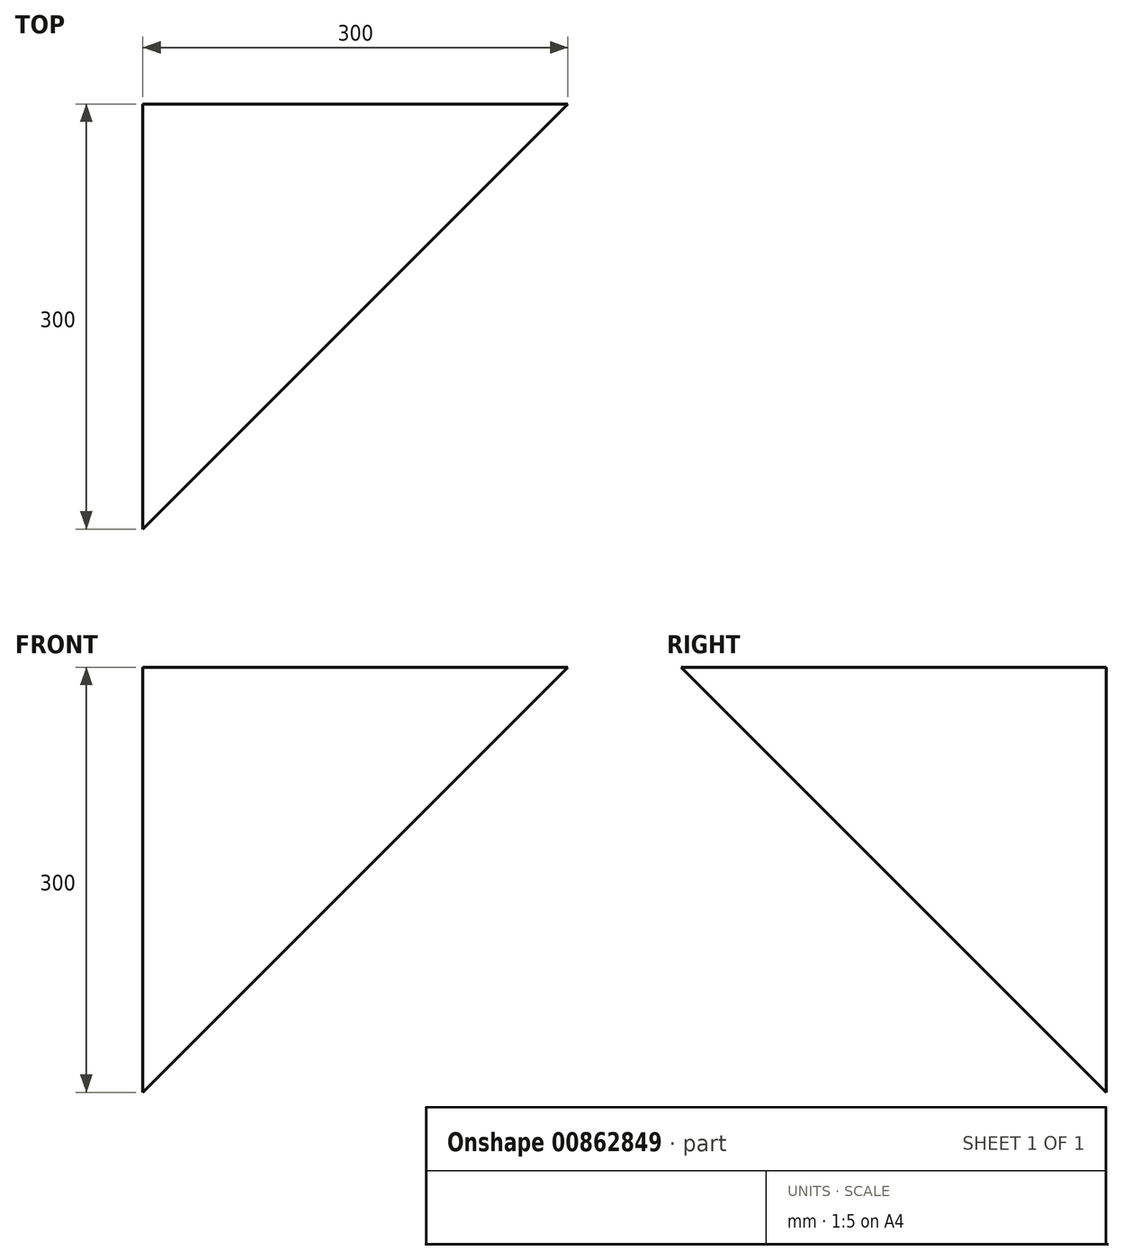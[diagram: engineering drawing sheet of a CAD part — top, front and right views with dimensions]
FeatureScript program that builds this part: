
annotation { "Feature Type Name" : "Feature", "Feature Type Description" : "" }
export const myFeature = defineFeature(function(context is Context, id is Id, definition is map)
    precondition{}
    {
        {
            var Q0;
            Q0=qCreatedBy(makeId("Top.planeOp"),FACE);
            var sketch = newSketch(context, id + "F0", { "sketchPlane" : qUnion([Q0])});
            skLineSegment(sketch, "E0.bottom", {"start": v(0, 0) * mm, "end": v(300, 0) * mm});
            skLineSegment(sketch, "E0.left", {"start": v(0, 0) * mm, "end": v(0, -300) * mm});
            skLineSegment(sketch, "E1", {"start": v(300, 0) * mm, "end": v(2300, 0) * mm});
            skLineSegment(sketch, "E2", {"start": v(0, -300) * mm, "end": v(0, -2300) * mm});
            skSolve(sketch);
        }
        {
            var Q0;
            Q0=qCreatedBy(makeId("Front.planeOp"),FACE);
            var sketch = newSketch(context, id + "F1", { "sketchPlane" : qUnion([Q0])});
            skLineSegment(sketch, "E3.0", {"start": v(0, 0) * mm, "end": v(300, 0) * mm});
            skLineSegment(sketch, "E4", {"start": v(0, 0) * mm, "end": v(0, -300) * mm});
            skLineSegment(sketch, "E5", {"start": v(0, -300) * mm, "end": v(0, -2300) * mm});
            skSolve(sketch);
        }
        {
            var Q0;
            Q0=sQuery(id+"F0.wireOp",VERTEX,"E0.left.end");
            var Q1;
            Q1=sQuery(id+"F0.wireOp",VERTEX,"E0.bottom.end");
            var Q2;
            Q2=sQuery(id+"F1.wireOp",VERTEX,"E4.end");
            cPlane(context, id + "F2", {"entities" : qUnion([Q0, Q1, Q2]), "cplaneType" : CPlaneType.THREE_POINT, "offset" : 25 * mm, "width" : 150 * mm, "height" : 150 * mm});
        }
        {
            var Q0;
            Q0=qCreatedBy(id+"F2.planeOp",FACE);
            var sketch = newSketch(context, id + "F3", { "sketchPlane" : qUnion([Q0])});
            skPoint(sketch, "E6.0", {"position": v(244.95, 0) * mm});
            skPoint(sketch, "E7.0", {"position": v(-122.47, 212.13) * mm});
            skPoint(sketch, "E8.0", {"position": v(-122.47, -212.13) * mm});
            skLineSegment(sketch, "E9", {"start": v(244.95, 0) * mm, "end": v(-122.47, -212.13) * mm});
            skLineSegment(sketch, "E10", {"start": v(-122.47, 212.13) * mm, "end": v(-122.47, -212.13) * mm});
            skLineSegment(sketch, "E11", {"start": v(-122.47, 212.13) * mm, "end": v(244.95, 0) * mm});
            skSolve(sketch);
        }
        {
            var Q0;
            Q0=makeQuery(id+"F3.imprint","IMPRINT",FACE,{"disambiguationData":[TD([[makeQuery(id+"F3.imprint","IMPRINT",EDGE,{"derivedFrom":sQuery(id+"F3.wireOp",EDGE,"E9")}),-1.0]])]});
            var Q1;
            Q1=sQuery(id+"F0.wireOp",VERTEX,"E0.bottom.start");
            loft(context, id + "F4", {"sheetProfilesArray" : [{ "sheetProfileEntities" : qUnion([Q0]) }, { "sheetProfileEntities" : qUnion([Q1]) }]});
        }
    });
